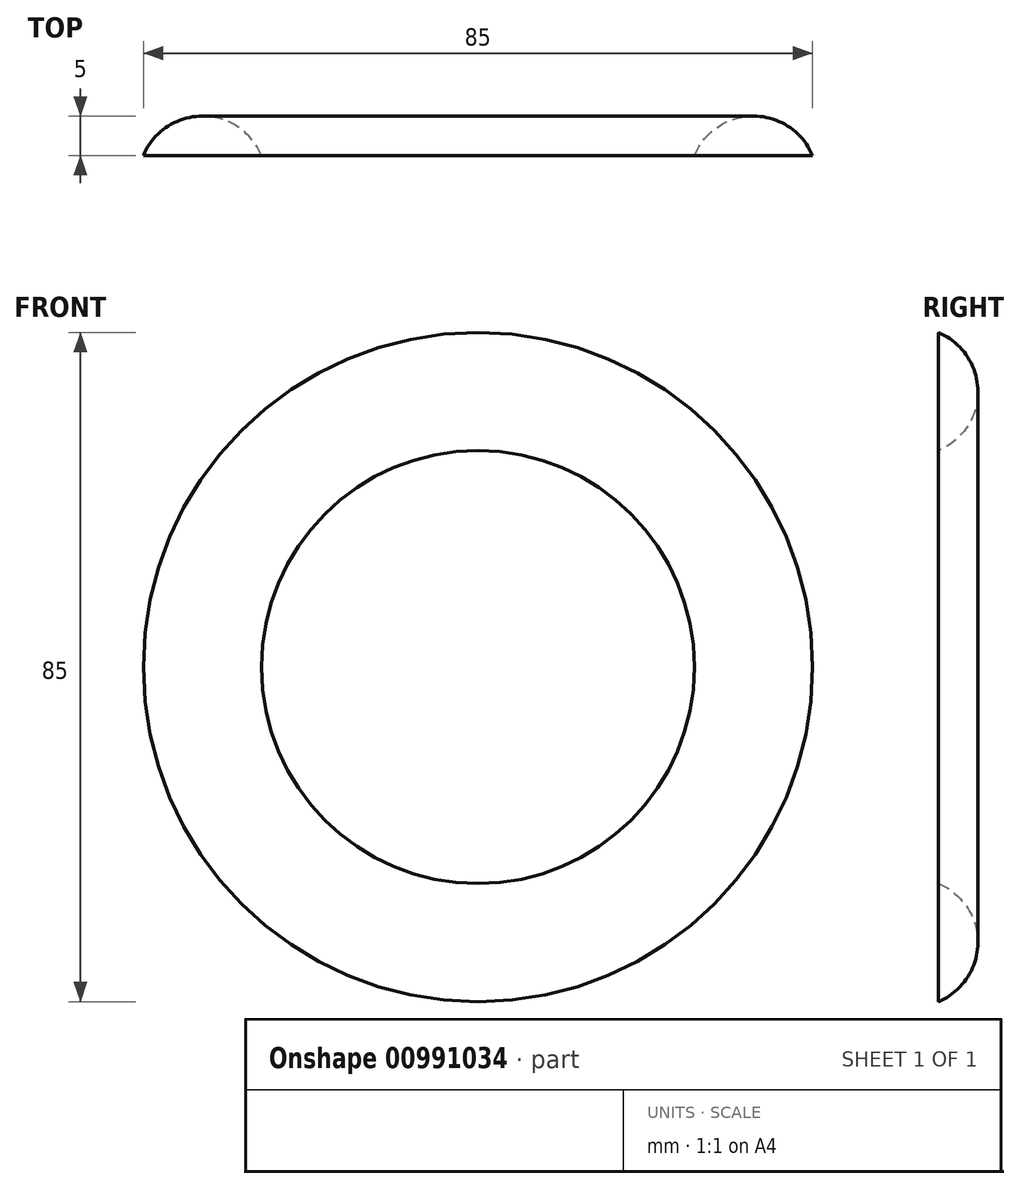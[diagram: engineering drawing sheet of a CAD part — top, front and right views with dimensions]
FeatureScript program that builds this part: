
annotation { "Feature Type Name" : "Feature", "Feature Type Description" : "" }
export const myFeature = defineFeature(function(context is Context, id is Id, definition is map)
    precondition{}
    {
        {
            var Q0;
            Q0=qCreatedBy(makeId("Front.planeOp"),FACE);
            var sketch = newSketch(context, id + "F0", { "sketchPlane" : qUnion([Q0])});
            skCircle(sketch, "E0", {"center": v(0, 0) * mm, "radius": 35 * mm, "construction": true});
            skCircle(sketch, "E1.0", {"center": v(0, 0) * mm, "radius": 42.5 * mm});
            skCircle(sketch, "E2.0", {"center": v(0, 0) * mm, "radius": 27.5 * mm});
            skLineSegment(sketch, "E3", {"start": v(0, 0) * mm, "end": v(0, 42.5) * mm, "construction": true});
            skPoint(sketch, "E4", {"position": v(0, 27.5) * mm});
            skSolve(sketch);
        }
        {
            var Q0;
            Q0=qCreatedBy(makeId("Right.planeOp"),FACE);
            var sketch = newSketch(context, id + "F1", { "sketchPlane" : qUnion([Q0])});
            skLineSegment(sketch, "E5.0", {"start": v(0, -42.5) * mm, "end": v(0, 42.5) * mm, "construction": true});
            skPoint(sketch, "E6.0", {"position": v(0, 27.5) * mm});
            skArc(sketch, "E7", {"start": v(0, 27.5) * mm, "mid": v(5, 35) * mm, "end": v(0, 42.5) * mm});
            skPoint(sketch, "E7.third.point", {"position": v(-11.14, 36.34) * mm});
            skLineSegment(sketch, "E8", {"start": v(0, 42.5) * mm, "end": v(0, 27.5) * mm});
            skSolve(sketch);
        }
        {
            var Q0;
            Q0=makeQuery(id+"F1.imprint","IMPRINT",FACE,{"disambiguationData":[TD([[makeQuery(id+"F1.imprint","IMPRINT",EDGE,{"derivedFrom":sQuery(id+"F1.wireOp",EDGE,"E7")}),1.0]])]});
            var Q1;
            Q1=sQuery(id+"F0.wireOp",EDGE,"E2.0");
            revolve(context, id + "F2", {"surfaceOperationType" : NewSurfaceOperationType.NEW, "entities" : qUnion([Q0]), "axis" : qUnion([Q1]), "revolveType" : RevolveType.FULL});
        }
    });
